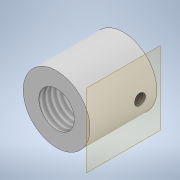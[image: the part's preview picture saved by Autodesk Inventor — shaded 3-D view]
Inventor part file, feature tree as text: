
AUTODESK INVENTOR PART (.ipt)
format: ipt  version: 2021.3 (Build 253353000, 353)  size: 137,728 bytes
history: native  units: mm
features: thread x2, sketch x2, revolve x1, plane x1, hole x1
ambient origin geometry x8: Origin, YZ Plane, XZ Plane, XY Plane, X Axis, Y Axis, Z Axis, Center Point
bodies: Volumenkörper1 (feature_tree)
feature tree (7):
  revolve  "Umdrehung1"
  thread  "Gewinde1"  [1 undecoded]
  thread  "Gewinde2"  [1 undecoded]
  plane  "Arbeitsebene1"
  hole  "Bohrung1"  [1 undecoded]
  sketch  "Skizze1"  dims[d9=4.5mm d10=5.0mm]
  sketch  "Skizze3"  dims[d11=5.0mm d12=0.0mm d13=7.5mm d14=0.0mm d15=6.0mm d16=15.0mm d17=7.5mm d18=15.0mm d19=7.5mm d20=3.75mm d22=2.459mm d23=6.0mm d24=4.0mm d25=2.0mm d26=90.0deg d27=8.0mm d28=20.594885mm]
note: 3 required parameter values undecoded (feature->parameter linkage not recoverable at this tier; creation-order binding heuristic only, values carry confidence <= 0.55)
